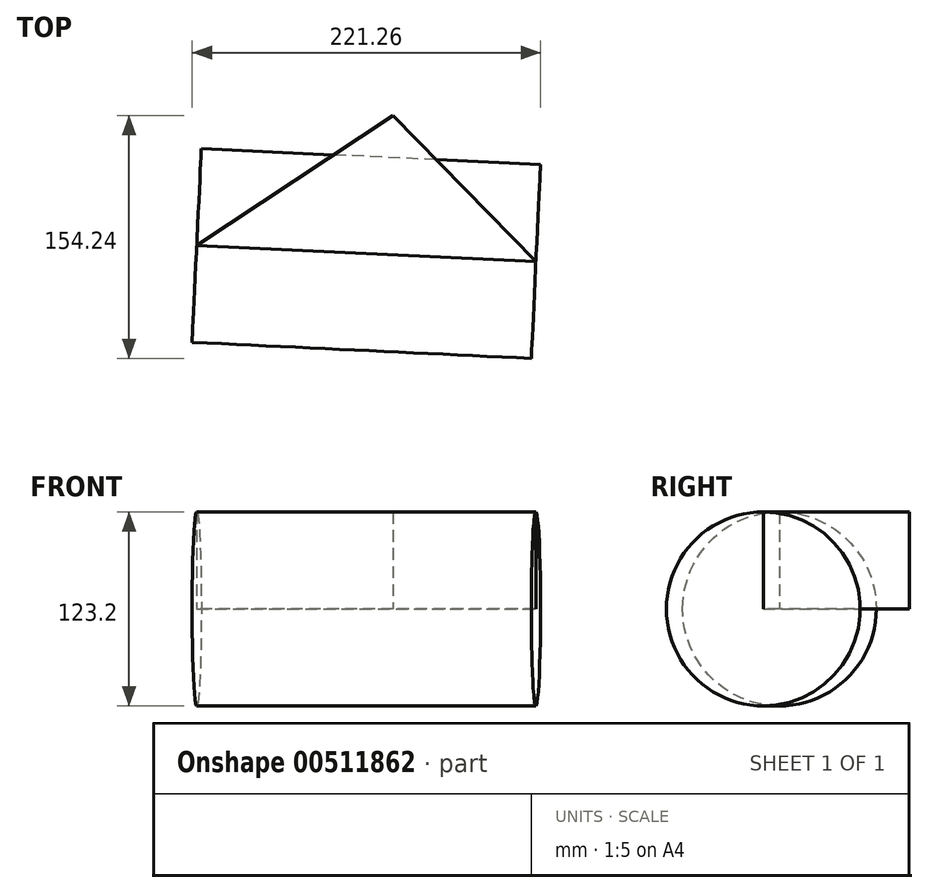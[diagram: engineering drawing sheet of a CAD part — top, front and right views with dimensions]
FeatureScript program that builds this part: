
annotation { "Feature Type Name" : "Feature", "Feature Type Description" : "" }
export const myFeature = defineFeature(function(context is Context, id is Id, definition is map)
    precondition{}
    {
        {
            var Q0;
            Q0=qCreatedBy(makeId("Top.planeOp"),FACE);
            var sketch = newSketch(context, id + "F0", { "sketchPlane" : qUnion([Q0])});
            skLineSegment(sketch, "E0", {"start": v(-100.53, -17.71) * mm, "end": v(114.87, -27.97) * mm});
            skLineSegment(sketch, "E1", {"start": v(114.87, -27.97) * mm, "end": v(24.2, 64.74) * mm});
            skLineSegment(sketch, "E2", {"start": v(24.2, 64.74) * mm, "end": v(-100.53, -17.71) * mm});
            skSolve(sketch);
        }
        {
            var Q0;
            Q0=makeQuery(id+"F0.imprint","IMPRINT",FACE,{"disambiguationData":[TD([[makeQuery(id+"F0.imprint","IMPRINT",EDGE,{"derivedFrom":sQuery(id+"F0.wireOp",EDGE,"E0")}),1.0]])]});
            extrude(context, id + "F1", {"entities" : qUnion([Q0]), "depth" : 61.6 * mm});
        }
        {
            var Q0;
            Q0=makeQuery(id+"F1.opExtrude","SWEPT_FACE",FACE,{"disambiguationData":[OSD([sQuery(id+"F0.wireOp",EDGE,"E0")])]});
            var Q1;
            Q1=makeQuery(id+"F1.opExtrude","CAP_EDGE",EDGE,{"disambiguationData":[OSD([sQuery(id+"F0.wireOp",EDGE,"E0")])],"isStart":true});
            revolve(context, id + "F2", {"entities" : qUnion([Q0]), "axis" : qUnion([Q1]), "revolveType" : RevolveType.FULL});
        }
    });
